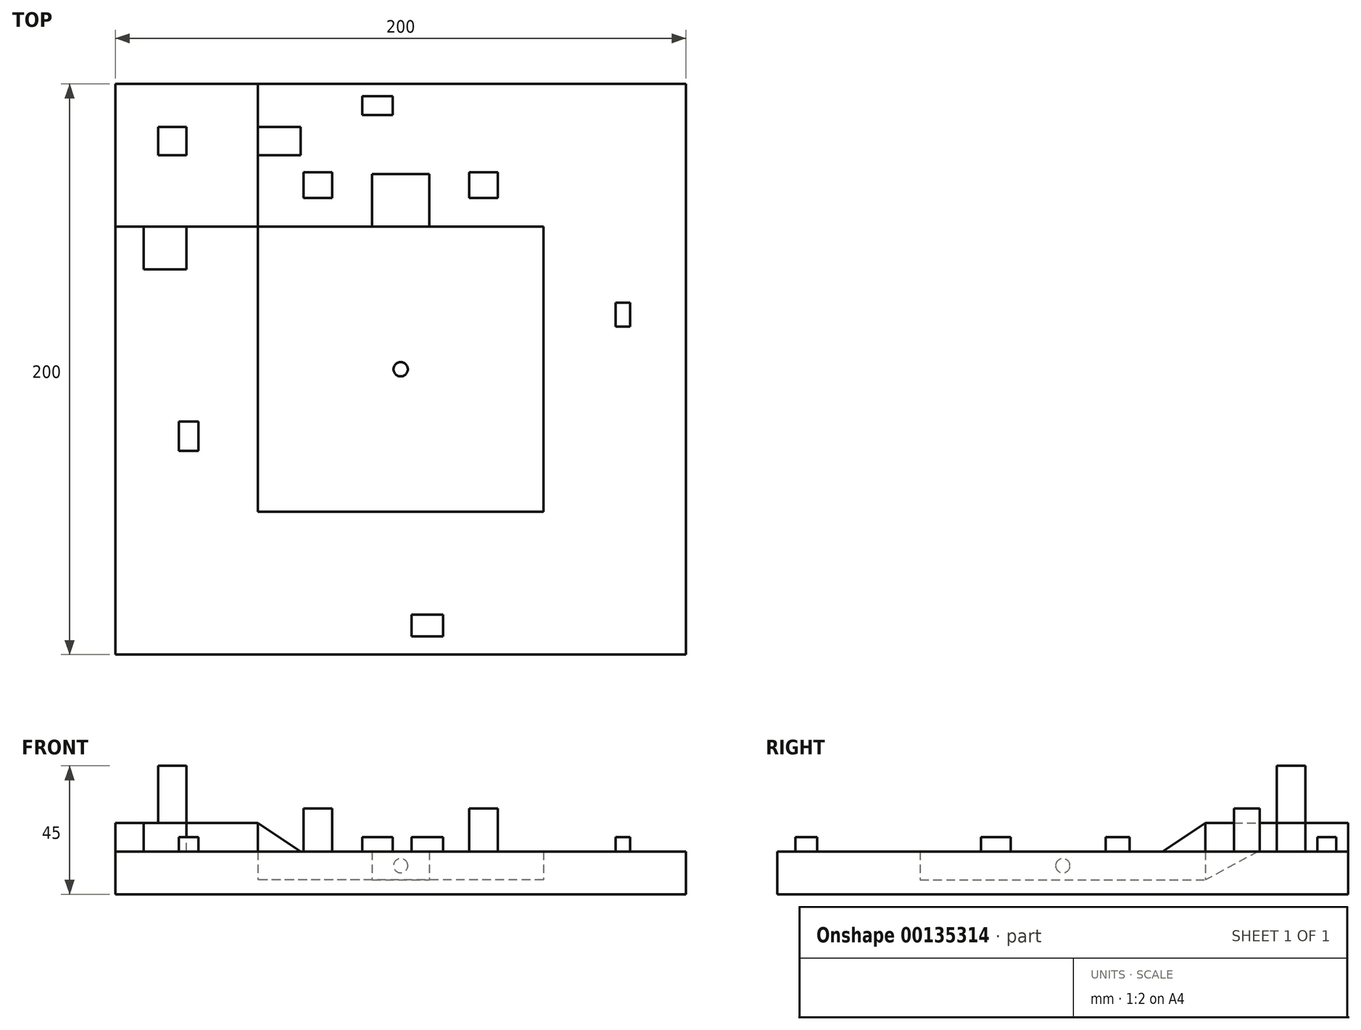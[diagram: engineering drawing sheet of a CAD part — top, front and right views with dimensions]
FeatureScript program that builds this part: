
annotation { "Feature Type Name" : "Feature", "Feature Type Description" : "" }
export const myFeature = defineFeature(function(context is Context, id is Id, definition is map)
    precondition{}
    {
        {
            var Q0;
            Q0=qCreatedBy(makeId("Top.planeOp"),FACE);
            var sketch = newSketch(context, id + "F0", { "sketchPlane" : qUnion([Q0])});
            skLineSegment(sketch, "E0.bottom", {"start": v(50, -50) * mm, "end": v(-50, -50) * mm});
            skLineSegment(sketch, "E0.top", {"start": v(50, 50) * mm, "end": v(-50, 50) * mm});
            skLineSegment(sketch, "E0.left", {"start": v(50, -50) * mm, "end": v(50, 50) * mm});
            skLineSegment(sketch, "E0.right", {"start": v(-50, -50) * mm, "end": v(-50, 50) * mm});
            skPoint(sketch, "E0.middle", {"position": v(0, 0) * mm});
            skLineSegment(sketch, "E1.bottom", {"start": v(100, -100) * mm, "end": v(-100, -100) * mm});
            skLineSegment(sketch, "E1.top", {"start": v(100, 100) * mm, "end": v(-100, 100) * mm});
            skLineSegment(sketch, "E1.left", {"start": v(100, -100) * mm, "end": v(100, 100) * mm});
            skLineSegment(sketch, "E1.right", {"start": v(-100, -100) * mm, "end": v(-100, 100) * mm});
            skSolve(sketch);
        }
        {
            var Q0;
            Q0=makeQuery(id+"F0.imprint","IMPRINT",FACE,{"disambiguationData":[TD([[makeQuery(id+"F0.imprint","IMPRINT",EDGE,{"derivedFrom":sQuery(id+"F0.wireOp",EDGE,"E0.bottom")}),1.0]])]});
            extrude(context, id + "F1", {"entities" : qUnion([Q0]), "depth" : 10 * mm});
        }
        {
            var Q0;
            Q0=makeQuery(id+"F1.opExtrude","CAP_FACE",FACE,{"disambiguationData":[OSD([sQuery(id+"F0.wireOp",EDGE,"E0.bottom"),sQuery(id+"F0.wireOp",EDGE,"E0.top"),sQuery(id+"F0.wireOp",EDGE,"E0.left"),sQuery(id+"F0.wireOp",EDGE,"E0.right"),sQuery(id+"F0.wireOp",EDGE,"E1.bottom"),sQuery(id+"F0.wireOp",EDGE,"E1.top"),sQuery(id+"F0.wireOp",EDGE,"E1.left"),sQuery(id+"F0.wireOp",EDGE,"E1.right")])],"isStart":true});
            var sketch = newSketch(context, id + "F2", { "sketchPlane" : qUnion([Q0])});
            skLineSegment(sketch, "E2.bottom", {"start": v(-100, 100) * mm, "end": v(100, 100) * mm});
            skLineSegment(sketch, "E2.top", {"start": v(-100, -100) * mm, "end": v(100, -100) * mm});
            skLineSegment(sketch, "E2.left", {"start": v(-100, 100) * mm, "end": v(-100, -100) * mm});
            skLineSegment(sketch, "E2.right", {"start": v(100, 100) * mm, "end": v(100, -100) * mm});
            skSolve(sketch);
        }
        {
            var Q0;
            Q0 = qSketchRegion(id + "F2", true);
            extrude(context, id + "F3", {"entities" : qUnion([Q0]), "operationType" : NewBodyOperationType.ADD, "depth" : 5 * mm});
        }
        {
            var Q0;
            Q0=qCreatedBy(makeId("Right.planeOp"),FACE);
            var sketch = newSketch(context, id + "F4", { "sketchPlane" : qUnion([Q0])});
            skLineSegment(sketch, "E3.0", {"start": v(50, 10) * mm, "end": v(68.4, 10) * mm});
            skLineSegment(sketch, "E4", {"start": v(50, 10) * mm, "end": v(50, 0) * mm});
            skLineSegment(sketch, "E5", {"start": v(68.4, 10) * mm, "end": v(50, 0) * mm});
            skSolve(sketch);
        }
        {
            var Q0;
            Q0 = qSketchRegion(id + "F4", true);
            var Q1;
            Q1=sQuery(id+"F4.wireOp",EDGE,"E5");
            var Q2;
            Q2=sQuery(id+"F4.wireOp",EDGE,"E3.0");
            var Q3;
            Q3=sQuery(id+"F4.wireOp",EDGE,"E4");
            extrude(context, id + "F5", {"entities" : qUnion([Q0]), "operationType" : NewBodyOperationType.REMOVE, "surfaceEntities" : qUnion([Q1, Q2, Q3]), "oppositeDirection" : true, "depth" : 10 * mm, "hasSecondDirection" : true, "secondDirectionOppositeDirection" : false, "secondDirectionDepth" : 10 * mm});
        }
        {
            var Q0;
            Q0=qCreatedBy(makeId("Right.planeOp"),FACE);
            var sketch = newSketch(context, id + "F6", { "sketchPlane" : qUnion([Q0])});
            skLineSegment(sketch, "E6", {"start": v(0, 0) * mm, "end": v(0, 75.28) * mm, "construction": true});
            skSolve(sketch);
        }
        {
            var Q0;
            Q0=makeQuery(id+"F1.opExtrude","CAP_FACE",FACE,{"disambiguationData":[OSD([sQuery(id+"F0.wireOp",EDGE,"E0.bottom"),sQuery(id+"F0.wireOp",EDGE,"E0.top"),sQuery(id+"F0.wireOp",EDGE,"E0.left"),sQuery(id+"F0.wireOp",EDGE,"E0.right"),sQuery(id+"F0.wireOp",EDGE,"E1.bottom"),sQuery(id+"F0.wireOp",EDGE,"E1.top"),sQuery(id+"F0.wireOp",EDGE,"E1.left"),sQuery(id+"F0.wireOp",EDGE,"E1.right")])],"isStart":false});
            var sketch = newSketch(context, id + "F7", { "sketchPlane" : qUnion([Q0])});
            skLineSegment(sketch, "E7.bottom", {"start": v(-50, 50) * mm, "end": v(-100, 50) * mm});
            skLineSegment(sketch, "E7.top", {"start": v(-50, 100) * mm, "end": v(-100, 100) * mm});
            skLineSegment(sketch, "E7.left", {"start": v(-50, 50) * mm, "end": v(-50, 100) * mm});
            skLineSegment(sketch, "E7.right", {"start": v(-100, 50) * mm, "end": v(-100, 100) * mm});
            skSolve(sketch);
        }
        {
            var Q0;
            Q0 = qSketchRegion(id + "F7", true);
            extrude(context, id + "F8", {"entities" : qUnion([Q0]), "operationType" : NewBodyOperationType.ADD, "depth" : 10 * mm});
        }
        {
            var Q0;
            Q0=makeQuery(id+"F8.opExtrude","CAP_FACE",FACE,{"disambiguationData":[OSD([sQuery(id+"F7.wireOp",EDGE,"E7.bottom"),sQuery(id+"F7.wireOp",EDGE,"E7.top"),sQuery(id+"F7.wireOp",EDGE,"E7.left"),sQuery(id+"F7.wireOp",EDGE,"E7.right")])],"isStart":false});
            var sketch = newSketch(context, id + "F9", { "sketchPlane" : qUnion([Q0])});
            skLineSegment(sketch, "E8", {"start": v(-100, 100) * mm, "end": v(-50, 50) * mm, "construction": true});
            skLineSegment(sketch, "E9", {"start": v(-50, 50) * mm, "end": v(-50, 100) * mm, "construction": true});
            skLineSegment(sketch, "E10", {"start": v(-50, 100) * mm, "end": v(-100, 50) * mm, "construction": true});
            skLineSegment(sketch, "E11", {"start": v(-75, 75) * mm, "end": v(-75, 23.4) * mm, "construction": true});
            skLineSegment(sketch, "E12", {"start": v(-75, 75) * mm, "end": v(-18.27, 75) * mm, "construction": true});
            skLineSegment(sketch, "E13.bottom", {"start": v(-75, 75) * mm, "end": v(-85, 75) * mm});
            skLineSegment(sketch, "E13.top", {"start": v(-75, 85) * mm, "end": v(-85, 85) * mm});
            skLineSegment(sketch, "E13.left", {"start": v(-75, 75) * mm, "end": v(-75, 85) * mm});
            skLineSegment(sketch, "E13.right", {"start": v(-85, 75) * mm, "end": v(-85, 85) * mm});
            skSolve(sketch);
        }
        {
            var Q0;
            Q0=sQuery(id+"F9.wireOp",EDGE,"E12");
            cPlane(context, id + "F10", {"entities" : qUnion([Q0]), "cplaneType" : CPlaneType.LINE_ANGLE, "offset" : 25 * mm, "angle" : 0 * degree, "width" : 150 * mm, "height" : 150 * mm});
        }
        {
            var Q0;
            Q0=qCreatedBy(id+"F10.planeOp",FACE);
            var sketch = newSketch(context, id + "F11", { "sketchPlane" : qUnion([Q0])});
            skLineSegment(sketch, "E14.0", {"start": v(50, 20) * mm, "end": v(50, 10) * mm});
            skLineSegment(sketch, "E15", {"start": v(50, 10) * mm, "end": v(35, 10) * mm});
            skLineSegment(sketch, "E16", {"start": v(35, 10) * mm, "end": v(50, 20) * mm});
            skSolve(sketch);
        }
        {
            var Q0;
            Q0=makeQuery(id+"F11.imprint","IMPRINT",FACE,{"disambiguationData":[TD([[makeQuery(id+"F11.imprint","IMPRINT",EDGE,{"derivedFrom":sQuery(id+"F11.wireOp",EDGE,"E14.0")}),-1.0]])]});
            extrude(context, id + "F12", {"entities" : qUnion([Q0]), "operationType" : NewBodyOperationType.ADD, "depth" : 10 * mm});
        }
        {
            var Q0;
            Q0=sQuery(id+"F9.wireOp",EDGE,"E11");
            cPlane(context, id + "F13", {"entities" : qUnion([Q0]), "cplaneType" : CPlaneType.LINE_ANGLE, "offset" : 25 * mm, "angle" : 90 * degree, "width" : 150 * mm, "height" : 150 * mm});
        }
        {
            var Q0;
            Q0=qCreatedBy(id+"F13.planeOp",FACE);
            var sketch = newSketch(context, id + "F14", { "sketchPlane" : qUnion([Q0])});
            skLineSegment(sketch, "E17.0", {"start": v(50, 20) * mm, "end": v(50, 10) * mm});
            skLineSegment(sketch, "E18", {"start": v(50, 10) * mm, "end": v(35, 10) * mm});
            skLineSegment(sketch, "E19", {"start": v(35, 10) * mm, "end": v(50, 20) * mm});
            skSolve(sketch);
        }
        {
            var Q0;
            Q0=makeQuery(id+"F14.imprint","IMPRINT",FACE,{"disambiguationData":[TD([[makeQuery(id+"F14.imprint","IMPRINT",EDGE,{"derivedFrom":sQuery(id+"F14.wireOp",EDGE,"E17.0")}),-1.0]])]});
            extrude(context, id + "F15", {"entities" : qUnion([Q0]), "operationType" : NewBodyOperationType.ADD, "oppositeDirection" : true, "depth" : 15 * mm});
        }
        {
            var Q0;
            Q0=qCreatedBy(makeId("Right.planeOp"),FACE);
            var sketch = newSketch(context, id + "F16", { "sketchPlane" : qUnion([Q0])});
            skLineSegment(sketch, "E20", {"start": v(0, 0) * mm, "end": v(0, 75.44) * mm, "construction": true});
            skSolve(sketch);
        }
        {
            var Q0;
            Q0=makeQuery(id+"F9.imprint","IMPRINT",FACE,{"disambiguationData":[TD([[makeQuery(id+"F9.imprint","IMPRINT",EDGE,{"derivedFrom":sQuery(id+"F9.wireOp",EDGE,"E13.bottom")}),-1.0]])]});
            extrude(context, id + "F17", {"entities" : qUnion([Q0]), "operationType" : NewBodyOperationType.ADD, "depth" : 20 * mm});
        }
        {
            var Q0;
            Q0=makeQuery(id+"F1.opExtrude","CAP_FACE",FACE,{"disambiguationData":[OSD([sQuery(id+"F0.wireOp",EDGE,"E0.bottom"),sQuery(id+"F0.wireOp",EDGE,"E0.top"),sQuery(id+"F0.wireOp",EDGE,"E0.left"),sQuery(id+"F0.wireOp",EDGE,"E0.right"),sQuery(id+"F0.wireOp",EDGE,"E1.bottom"),sQuery(id+"F0.wireOp",EDGE,"E1.top"),sQuery(id+"F0.wireOp",EDGE,"E1.left"),sQuery(id+"F0.wireOp",EDGE,"E1.right")])],"isStart":false});
            var sketch = newSketch(context, id + "F18", { "sketchPlane" : qUnion([Q0])});
            skLineSegment(sketch, "E21", {"start": v(0, 43.73) * mm, "end": v(0, 77.59) * mm, "construction": true});
            skLineSegment(sketch, "E22.0", {"start": v(-10, 50) * mm, "end": v(-10, 68.4) * mm, "construction": true});
            skLineSegment(sketch, "E23.0", {"start": v(-10, 50) * mm, "end": v(-50, 50) * mm, "construction": true});
            skLineSegment(sketch, "E24.bottom", {"start": v(-34, 69) * mm, "end": v(-24, 69) * mm});
            skLineSegment(sketch, "E24.top", {"start": v(-34, 60) * mm, "end": v(-24, 60) * mm});
            skLineSegment(sketch, "E24.left", {"start": v(-34, 69) * mm, "end": v(-34, 60) * mm});
            skLineSegment(sketch, "E24.right", {"start": v(-24, 69) * mm, "end": v(-24, 60) * mm});
            skLineSegment(sketch, "E25.MirrorCS", {"start": v(34, 69) * mm, "end": v(34, 60) * mm});
            skLineSegment(sketch, "E26.MirrorCS", {"start": v(34, 69) * mm, "end": v(24, 69) * mm});
            skLineSegment(sketch, "E27.MirrorCS", {"start": v(34, 60) * mm, "end": v(24, 60) * mm});
            skLineSegment(sketch, "E28.MirrorCS", {"start": v(24, 69) * mm, "end": v(24, 60) * mm});
            skSolve(sketch);
        }
        {
            var Q0;
            Q0=makeQuery(id+"F18.imprint","IMPRINT",FACE,{"disambiguationData":[TD([[makeQuery(id+"F18.imprint","IMPRINT",EDGE,{"derivedFrom":sQuery(id+"F18.wireOp",EDGE,"E24.bottom")}),-1.0]])]});
            var Q1;
            Q1=makeQuery(id+"F18.imprint","IMPRINT",FACE,{"disambiguationData":[TD([[makeQuery(id+"F18.imprint","IMPRINT",EDGE,{"derivedFrom":sQuery(id+"F18.wireOp",EDGE,"E25.MirrorCS")}),-1.0]])]});
            extrude(context, id + "F19", {"entities" : qUnion([Q0, Q1]), "operationType" : NewBodyOperationType.ADD, "depth" : 15 * mm});
        }
        {
            var Q0;
            Q0=qCreatedBy(makeId("Front.planeOp"),FACE);
            var sketch = newSketch(context, id + "F20", { "sketchPlane" : qUnion([Q0])});
            skLineSegment(sketch, "E29", {"start": v(0, 0) * mm, "end": v(0, 76.75) * mm, "construction": true});
            skSolve(sketch);
        }
        {
            var Q0;
            {var subQ8=sQuery(id+"F0.wireOp",EDGE,"E1.left");var subQ10=sQuery(id+"F0.wireOp",EDGE,"E0.bottom");var subQ11=makeQuery(id+"F1.opExtrude","SWEPT_FACE",FACE,{"disambiguationData":[OSD([subQ10])]});var subQ12=sQuery(id+"F0.wireOp",EDGE,"E1.top");var subQ13=sQuery(id+"F0.wireOp",EDGE,"E1.bottom");var subQ14=sQuery(id+"F0.wireOp",EDGE,"E0.right");var subQ15=sQuery(id+"F0.wireOp",EDGE,"E0.left");var subQ16=sQuery(id+"F0.wireOp",EDGE,"E0.top");var subQ17=makeQuery(id+"F1.opExtrude","CAP_FACE",FACE,{"disambiguationData":[OSD([subQ10,subQ16,subQ15,subQ14,subQ13,subQ12,subQ8,sQuery(id+"F0.wireOp",EDGE,"E1.right")])],"isStart":false});var subQ21=makeQuery(id+"F1.opExtrude","SWEPT_FACE",FACE,{"disambiguationData":[OSD([subQ16])]});var subQ23=makeQuery(id+"F1.opExtrude","SWEPT_FACE",FACE,{"disambiguationData":[OSD([subQ15])]});Q0=makeQuery(id+"FYrEG4aEJ6ghjxu_1.3.F8.boolean.opBoolean","SPLIT",FACE,{"disambiguationData":[TD([subQ11])],"derivedFrom":makeQuery(id+"FYrEG4aEJ6ghjxu_1.2.F8.boolean.opBoolean","SPLIT",FACE,{"disambiguationData":[TD([subQ21])],"derivedFrom":makeQuery(id+"FYrEG4aEJ6ghjxu_1.1.F8.boolean.opBoolean","SPLIT",FACE,{"disambiguationData":[TD([subQ23])],"derivedFrom":subQ17})})});}
            var sketch = newSketch(context, id + "F21", { "sketchPlane" : qUnion([Q0])});
            skLineSegment(sketch, "E30.bottom", {"start": v(75.26, 23.35) * mm, "end": v(80.44, 23.35) * mm});
            skLineSegment(sketch, "E30.top", {"start": v(75.26, 14.97) * mm, "end": v(80.44, 14.97) * mm});
            skLineSegment(sketch, "E30.left", {"start": v(75.26, 23.35) * mm, "end": v(75.26, 14.97) * mm});
            skLineSegment(sketch, "E30.right", {"start": v(80.44, 23.35) * mm, "end": v(80.44, 14.97) * mm});
            skLineSegment(sketch, "E31.bottom", {"start": v(-13.44, 95.79) * mm, "end": v(-2.84, 95.79) * mm});
            skLineSegment(sketch, "E31.top", {"start": v(-13.44, 89.14) * mm, "end": v(-2.84, 89.14) * mm});
            skLineSegment(sketch, "E31.left", {"start": v(-13.44, 95.79) * mm, "end": v(-13.44, 89.14) * mm});
            skLineSegment(sketch, "E31.right", {"start": v(-2.84, 95.79) * mm, "end": v(-2.84, 89.14) * mm});
            skLineSegment(sketch, "E32.bottom", {"start": v(-77.75, -18.29) * mm, "end": v(-70.85, -18.29) * mm});
            skLineSegment(sketch, "E32.top", {"start": v(-77.75, -28.64) * mm, "end": v(-70.85, -28.64) * mm});
            skLineSegment(sketch, "E32.left", {"start": v(-77.75, -18.29) * mm, "end": v(-77.75, -28.64) * mm});
            skLineSegment(sketch, "E32.right", {"start": v(-70.85, -18.29) * mm, "end": v(-70.85, -28.64) * mm});
            skLineSegment(sketch, "E33.bottom", {"start": v(3.8, -86.05) * mm, "end": v(14.9, -86.05) * mm});
            skLineSegment(sketch, "E33.top", {"start": v(3.8, -93.69) * mm, "end": v(14.9, -93.69) * mm});
            skLineSegment(sketch, "E33.left", {"start": v(3.8, -86.05) * mm, "end": v(3.8, -93.69) * mm});
            skLineSegment(sketch, "E33.right", {"start": v(14.9, -86.05) * mm, "end": v(14.9, -93.69) * mm});
            skSolve(sketch);
        }
        {
            var Q0;
            Q0 = qSketchRegion(id + "F21", true);
            extrude(context, id + "F22", {"entities" : qUnion([Q0]), "operationType" : NewBodyOperationType.ADD, "depth" : 5 * mm});
        }
        {
            var Q0;
            Q0=makeQuery(id+"F3.opExtrude","CAP_FACE",FACE,{"disambiguationData":[OSD([sQuery(id+"F2.wireOp",EDGE,"E2.bottom"),sQuery(id+"F2.wireOp",EDGE,"E2.top"),sQuery(id+"F2.wireOp",EDGE,"E2.left"),sQuery(id+"F2.wireOp",EDGE,"E2.right")])],"isStart":true});
            cPlane(context, id + "F23", {"entities" : qUnion([Q0]), "cplaneType" : CPlaneType.OFFSET, "offset" : 5 * mm, "width" : 150 * mm, "height" : 150 * mm});
        }
        {
            var Q0;
            Q0=qCreatedBy(id+"F23.planeOp",FACE);
            var sketch = newSketch(context, id + "F24", { "sketchPlane" : qUnion([Q0])});
            skArc(sketch, "E34", {"start": v(0, -2.5) * mm, "mid": v(2.5, 0) * mm, "end": v(0, 2.5) * mm});
            skLineSegment(sketch, "E35", {"start": v(0, 8.1) * mm, "end": v(0, -7.04) * mm, "construction": true});
            skLineSegment(sketch, "E36", {"start": v(0, -2.5) * mm, "end": v(0, 2.5) * mm});
            skSolve(sketch);
        }
        {
            var Q0;
            Q0=makeQuery(id+"F24.imprint","IMPRINT",FACE,{"disambiguationData":[TD([[makeQuery(id+"F24.imprint","IMPRINT",EDGE,{"derivedFrom":sQuery(id+"F24.wireOp",EDGE,"E34")}),1.0]])]});
            var Q1;
            Q1=sQuery(id+"F24.wireOp",EDGE,"E35");
            revolve(context, id + "F25", {"entities" : qUnion([Q0]), "axis" : qUnion([Q1]), "revolveType" : RevolveType.FULL});
        }
    });
